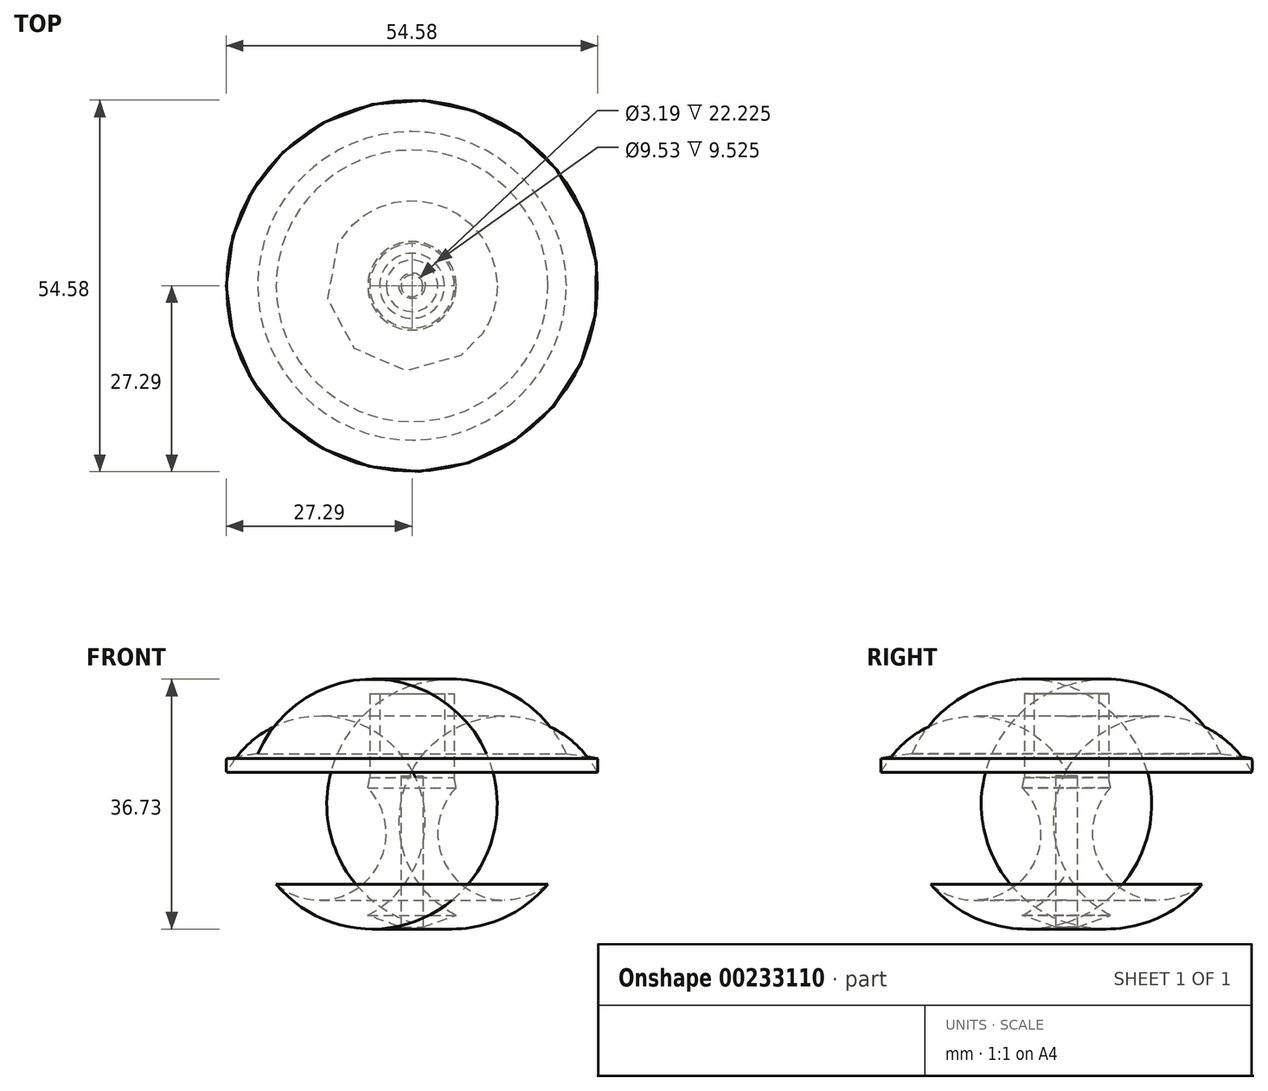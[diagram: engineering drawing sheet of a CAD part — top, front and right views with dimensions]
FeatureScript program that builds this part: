
annotation { "Feature Type Name" : "Feature", "Feature Type Description" : "" }
export const myFeature = defineFeature(function(context is Context, id is Id, definition is map)
    precondition{}
    {
        {
            var Q0;
            Q0=qCreatedBy(makeId("Front.planeOp"),FACE);
            var sketch = newSketch(context, id + "F0", { "sketchPlane" : qUnion([Q0])});
            skLineSegment(sketch, "E0", {"start": v(0, 22.8) * mm, "end": v(0, 25.33) * mm});
            skArc(sketch, "E1", {"start": v(27.23, 23.31) * mm, "mid": v(27.29, 24.35) * mm, "end": v(27.23, 25.39) * mm});
            skLineSegment(sketch, "E2.trimOffspring", {"start": v(22.67, 26.06) * mm, "end": v(27.23, 25.39) * mm});
            skLineSegment(sketch, "E3", {"start": v(1.6, 0.57) * mm, "end": v(6.49, 2.32) * mm});
            skArc(sketch, "E4", {"start": v(6.49, 2.32) * mm, "mid": v(24.55, 5.22) * mm, "end": v(27.23, 23.31) * mm});
            skArc(sketch, "E5", {"start": v(6.2, 22.59) * mm, "mid": v(6.33, 21.83) * mm, "end": v(6.48, 21.07) * mm});
            skArc(sketch, "E6", {"start": v(19.96, 6.9) * mm, "mid": v(24.04, 16.1) * mm, "end": v(22.67, 26.06) * mm});
            skArc(sketch, "E7", {"start": v(6.48, 21.07) * mm, "mid": v(6.49, 7.58) * mm, "end": v(19.96, 6.9) * mm});
            skLineSegment(sketch, "E8", {"start": v(0, 22.8) * mm, "end": v(1.6, 22.8) * mm});
            skLineSegment(sketch, "E9", {"start": v(1.6, 22.8) * mm, "end": v(1.6, 0.57) * mm});
            skLineSegment(sketch, "E10", {"start": v(4.76, 34.86) * mm, "end": v(4.76, 25.33) * mm});
            skLineSegment(sketch, "E11", {"start": v(4.76, 25.33) * mm, "end": v(0, 25.33) * mm});
            skLineSegment(sketch, "E12", {"start": v(6.2, 22.59) * mm, "end": v(6.2, 34.86) * mm});
            skLineSegment(sketch, "E13", {"start": v(6.2, 34.86) * mm, "end": v(4.76, 34.86) * mm});
            skPoint(sketch, "E14.orphan", {"position": v(0, 0) * mm});
            skPoint(sketch, "E15", {"position": v(7.12, 18.67) * mm});
            skPoint(sketch, "E16", {"position": v(24.16, 17.17) * mm});
            skPoint(sketch, "E17", {"position": v(4.8, 18.67) * mm});
            skPoint(sketch, "E18", {"position": v(12.85, 4.57) * mm});
            skPoint(sketch, "E19", {"position": v(22.67, 26.06) * mm});
            skSolve(sketch);
        }
        {
            var Q0;
            Q0 = qSketchRegion(id + "F0", true);
            var Q1;
            Q1=sQuery(id+"F0.wireOp",EDGE,"E0");
            revolve(context, id + "F1", {"entities" : qUnion([Q0]), "axis" : qUnion([Q1]), "revolveType" : RevolveType.FULL});
        }
    });
